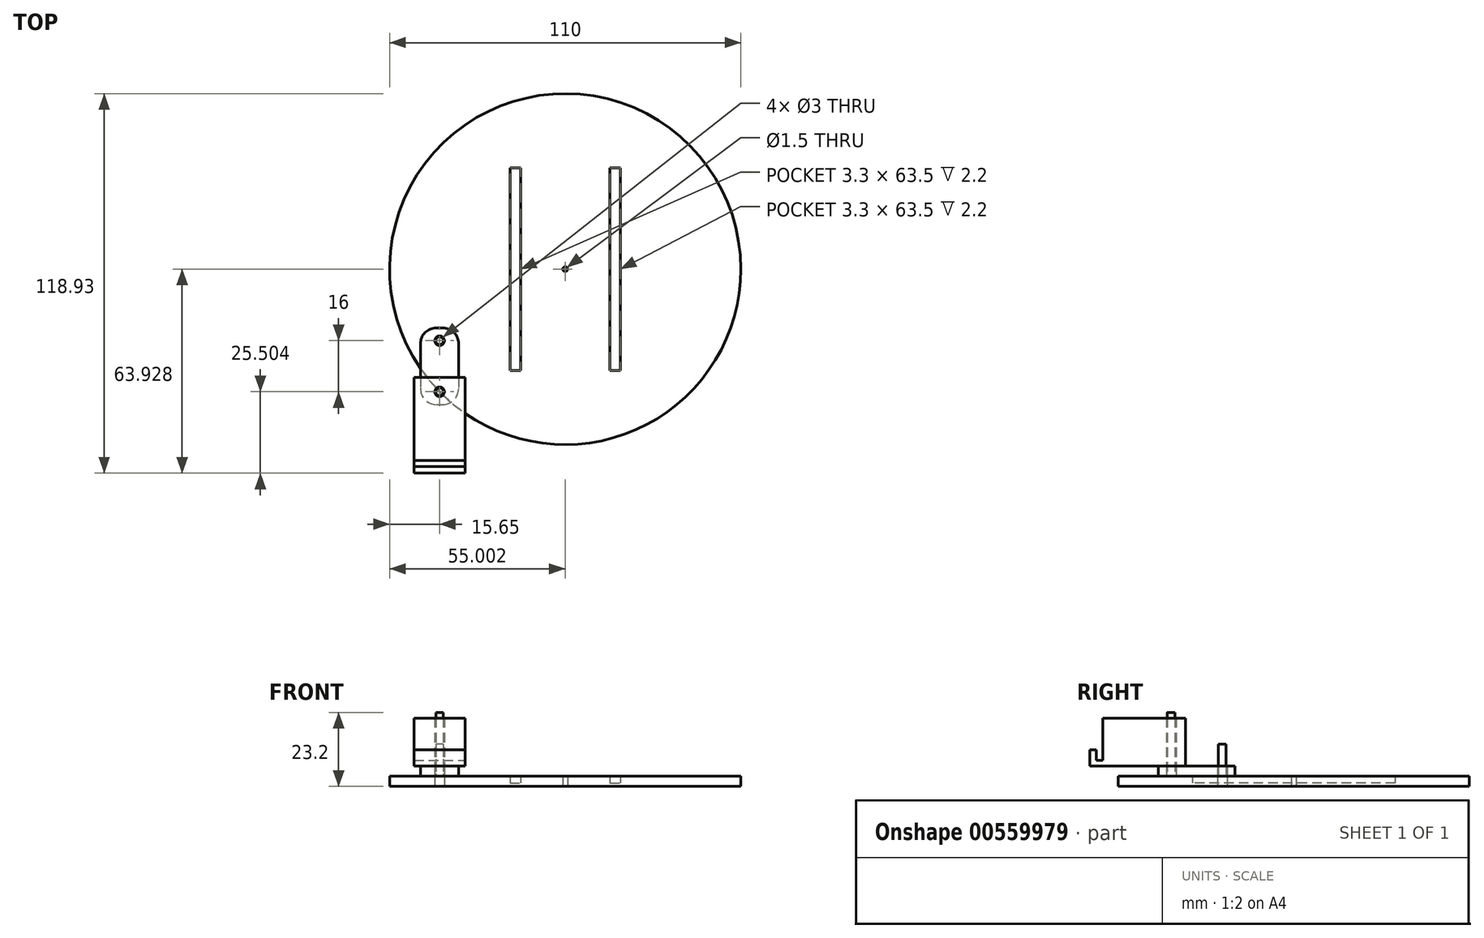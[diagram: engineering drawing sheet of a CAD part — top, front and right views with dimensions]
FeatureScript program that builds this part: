
annotation { "Feature Type Name" : "Feature", "Feature Type Description" : "" }
export const myFeature = defineFeature(function(context is Context, id is Id, definition is map)
    precondition{}
    {
        {
            var Q0;
            Q0=qCreatedBy(makeId("Top.planeOp"),FACE);
            var sketch = newSketch(context, id + "F0", { "sketchPlane" : qUnion([Q0])});
            skCircle(sketch, "E0", {"center": v(39.35, 117.44) * mm, "radius": 55 * mm});
            skCircle(sketch, "E1", {"center": v(0, 95.01) * mm, "radius": 1.5 * mm});
            skCircle(sketch, "E2", {"center": v(39.35, 117.44) * mm, "radius": 0.75 * mm});
            skLineSegment(sketch, "E3.bottom", {"start": v(22.05, 149.19) * mm, "end": v(25.35, 149.19) * mm});
            skLineSegment(sketch, "E3.top", {"start": v(22.05, 85.69) * mm, "end": v(25.35, 85.69) * mm});
            skLineSegment(sketch, "E3.left", {"start": v(22.05, 149.19) * mm, "end": v(22.05, 85.69) * mm});
            skLineSegment(sketch, "E3.right", {"start": v(25.35, 149.19) * mm, "end": v(25.35, 85.69) * mm});
            skLineSegment(sketch, "E4.bottom", {"start": v(53.35, 149.19) * mm, "end": v(56.65, 149.19) * mm});
            skLineSegment(sketch, "E4.top", {"start": v(53.35, 85.69) * mm, "end": v(56.65, 85.69) * mm});
            skLineSegment(sketch, "E4.left", {"start": v(53.35, 149.19) * mm, "end": v(53.35, 85.69) * mm});
            skLineSegment(sketch, "E4.right", {"start": v(56.65, 149.19) * mm, "end": v(56.65, 85.69) * mm});
            skSolve(sketch);
        }
        {
            var Q0;
            Q0=makeQuery(id+"F0.imprint","IMPRINT",FACE,{"disambiguationData":[TD([[makeQuery(id+"F0.imprint","IMPRINT",EDGE,{"derivedFrom":sQuery(id+"F0.wireOp",EDGE,"E0")}),1.0]])]});
            extrude(context, id + "F1", {"entities" : qUnion([Q0]), "depth" : 3.2 * mm});
        }
        {
            var Q0;
            Q0=makeQuery(id+"F0.imprint","IMPRINT",FACE,{"disambiguationData":[TD([[makeQuery(id+"F0.imprint","IMPRINT",EDGE,{"derivedFrom":sQuery(id+"F0.wireOp",EDGE,"E3.bottom")}),-1.0]])]});
            var Q1;
            Q1=makeQuery(id+"F0.imprint","IMPRINT",FACE,{"disambiguationData":[TD([[makeQuery(id+"F0.imprint","IMPRINT",EDGE,{"derivedFrom":sQuery(id+"F0.wireOp",EDGE,"E4.bottom")}),-1.0]])]});
            extrude(context, id + "F2", {"entities" : qUnion([Q0, Q1]), "operationType" : NewBodyOperationType.ADD, "depth" : 1 * mm});
        }
        {
            var Q0;
            Q0=makeQuery(id+"F1.opExtrude","CAP_FACE",FACE,{"disambiguationData":[OSD([sQuery(id+"F0.wireOp",EDGE,"E0"),sQuery(id+"F0.wireOp",EDGE,"E1"),sQuery(id+"F0.wireOp",EDGE,"E2"),sQuery(id+"F0.wireOp",EDGE,"E3.bottom"),sQuery(id+"F0.wireOp",EDGE,"E3.top"),sQuery(id+"F0.wireOp",EDGE,"E3.left"),sQuery(id+"F0.wireOp",EDGE,"E3.right"),sQuery(id+"F0.wireOp",EDGE,"E4.bottom"),sQuery(id+"F0.wireOp",EDGE,"E4.top"),sQuery(id+"F0.wireOp",EDGE,"E4.left"),sQuery(id+"F0.wireOp",EDGE,"E4.right")])],"isStart":false});
            var sketch = newSketch(context, id + "F3", { "sketchPlane" : qUnion([Q0])});
            skCircle(sketch, "E5", {"center": v(0, 95.01) * mm, "radius": 1.2 * mm});
            skSolve(sketch);
        }
        {
            var Q0;
            Q0=makeQuery(id+"F3.imprint","IMPRINT",FACE,{"disambiguationData":[TD([[makeQuery(id+"F3.imprint","IMPRINT",EDGE,{"derivedFrom":sQuery(id+"F3.wireOp",EDGE,"E5")}),1.0]])]});
            extrude(context, id + "F4", {"entities" : qUnion([Q0]), "depth" : 10 * mm, "offsetDistance" : 25 * mm});
        }
        {
            var Q0;
            Q0=makeQuery(id+"F1.opExtrude","CAP_FACE",FACE,{"disambiguationData":[OSD([sQuery(id+"F0.wireOp",EDGE,"E0"),sQuery(id+"F0.wireOp",EDGE,"E1"),sQuery(id+"F0.wireOp",EDGE,"E2"),sQuery(id+"F0.wireOp",EDGE,"E3.bottom"),sQuery(id+"F0.wireOp",EDGE,"E3.top"),sQuery(id+"F0.wireOp",EDGE,"E3.left"),sQuery(id+"F0.wireOp",EDGE,"E3.right"),sQuery(id+"F0.wireOp",EDGE,"E4.bottom"),sQuery(id+"F0.wireOp",EDGE,"E4.top"),sQuery(id+"F0.wireOp",EDGE,"E4.left"),sQuery(id+"F0.wireOp",EDGE,"E4.right")])],"isStart":false});
            var sketch = newSketch(context, id + "F5", { "sketchPlane" : qUnion([Q0])});
            skLineSegment(sketch, "E6.bottom", {"start": v(-6, 99.01) * mm, "end": v(6, 99.01) * mm});
            skLineSegment(sketch, "E6.top", {"start": v(-6, 75.01) * mm, "end": v(6, 75.01) * mm});
            skLineSegment(sketch, "E6.left", {"start": v(-6, 99.01) * mm, "end": v(-6, 75.01) * mm});
            skLineSegment(sketch, "E6.right", {"start": v(6, 99.01) * mm, "end": v(6, 75.01) * mm});
            skCircle(sketch, "E7", {"center": v(0, 95.01) * mm, "radius": 1.5 * mm});
            skCircle(sketch, "E8", {"center": v(0, 79.01) * mm, "radius": 1.5 * mm});
            skSolve(sketch);
        }
        {
            var Q0;
            {var subQ4=sQuery(id+"F5.wireOp",EDGE,"E6.top");var subQ6=sQuery(id+"F5.wireOp",EDGE,"E6.left");var subQ7=makeQuery(id+"F5.imprint","INTERSECT",VERTEX,{"derivedFrom":[subQ4,subQ6]});Q0=makeQuery(id+"F5.imprint","IMPRINT",FACE,{"disambiguationData":[TD([[makeQuery(id+"F5.imprint","IMPRINT",EDGE,{"disambiguationData":[TD([[subQ7,-1.0]])],"derivedFrom":subQ4}),1.0]])]});}
            var Q1;
            {var subQ1=sQuery(id+"F5.wireOp",EDGE,"E6.bottom");Q1=makeQuery(id+"F5.imprint","IMPRINT",FACE,{"disambiguationData":[TD([[makeQuery(id+"F5.imprint","IMPRINT",EDGE,{"derivedFrom":subQ1}),-1.0]])]});}
            extrude(context, id + "F6", {"entities" : qUnion([Q0, Q1]), "depth" : 3.2 * mm, "offsetDistance" : 25 * mm});
        }
        {
            var Q0;
            Q0=makeQuery(id+"F6.opExtrude","SWEPT_EDGE",EDGE,{"disambiguationData":[OSD([sQuery(id+"F5.wireOp",EDGE,"E6.bottom"),sQuery(id+"F5.wireOp",EDGE,"E6.left")])]});
            var Q1;
            Q1=makeQuery(id+"F6.opExtrude","SWEPT_EDGE",EDGE,{"disambiguationData":[OSD([sQuery(id+"F5.wireOp",EDGE,"E6.bottom"),sQuery(id+"F5.wireOp",EDGE,"E6.right")])]});
            var Q2;
            Q2=makeQuery(id+"F6.opExtrude","SWEPT_EDGE",EDGE,{"disambiguationData":[OSD([sQuery(id+"F5.wireOp",EDGE,"E6.top"),sQuery(id+"F5.wireOp",EDGE,"E6.right")])]});
            var Q3;
            Q3=makeQuery(id+"F6.opExtrude","SWEPT_EDGE",EDGE,{"disambiguationData":[OSD([sQuery(id+"F5.wireOp",EDGE,"E6.top"),sQuery(id+"F5.wireOp",EDGE,"E6.left")])]});
            fillet(context, id + "F7", {"entities" : qUnion([Q0, Q1, Q2, Q3]), "radius" : 5 * mm, "tangentPropagation" : true, "allowEdgeOverflow" : false});
        }
        {
            var Q0;
            Q0=makeQuery(id+"F1.opExtrude","CAP_FACE",FACE,{"disambiguationData":[OSD([sQuery(id+"F0.wireOp",EDGE,"E0"),sQuery(id+"F0.wireOp",EDGE,"E1"),sQuery(id+"F0.wireOp",EDGE,"E2"),sQuery(id+"F0.wireOp",EDGE,"E3.bottom"),sQuery(id+"F0.wireOp",EDGE,"E3.top"),sQuery(id+"F0.wireOp",EDGE,"E3.left"),sQuery(id+"F0.wireOp",EDGE,"E3.right"),sQuery(id+"F0.wireOp",EDGE,"E4.bottom"),sQuery(id+"F0.wireOp",EDGE,"E4.top"),sQuery(id+"F0.wireOp",EDGE,"E4.left"),sQuery(id+"F0.wireOp",EDGE,"E4.right")])],"isStart":false});
            var sketch = newSketch(context, id + "F8", { "sketchPlane" : qUnion([Q0])});
            skCircle(sketch, "E9", {"center": v(0, 79.01) * mm, "radius": 1.2 * mm});
            skSolve(sketch);
        }
        {
            var Q0;
            {var subQ0=sQuery(id+"F8.wireOp",EDGE,"E9");var subQ1=makeQuery(id+"F1.opExtrude","CAP_EDGE",EDGE,{"disambiguationData":[OSD([sQuery(id+"F0.wireOp",EDGE,"E0")])],"isStart":false});var subQ2=makeQuery(id+"F8.imprint","INTERSECT",VERTEX,{"disambiguationData":[OD(0.0)],"derivedFrom":[subQ1,subQ0]});Q0=makeQuery(id+"F8.imprint","IMPRINT",FACE,{"disambiguationData":[TD([[makeQuery(id+"F8.imprint","IMPRINT",EDGE,{"disambiguationData":[TD([[subQ2,-1.0]])],"derivedFrom":subQ0}),1.0]])]});}
            var Q1;
            {var subQ0=sQuery(id+"F8.wireOp",EDGE,"E9");var subQ1=makeQuery(id+"F1.opExtrude","CAP_EDGE",EDGE,{"disambiguationData":[OSD([sQuery(id+"F0.wireOp",EDGE,"E0")])],"isStart":false});var subQ2=makeQuery(id+"F8.imprint","INTERSECT",VERTEX,{"disambiguationData":[OD(0.0)],"derivedFrom":[subQ1,subQ0]});Q1=makeQuery(id+"F8.imprint","IMPRINT",FACE,{"disambiguationData":[TD([[makeQuery(id+"F8.imprint","IMPRINT",EDGE,{"disambiguationData":[TD([[subQ2,1.0]])],"derivedFrom":subQ0}),1.0]])]});}
            extrude(context, id + "F9", {"entities" : qUnion([Q0, Q1]), "depth" : 20 * mm, "offsetDistance" : 25 * mm});
        }
        {
            var Q0;
            Q0=makeQuery(id+"F6.opExtrude","CAP_FACE",FACE,{"disambiguationData":[OSD([sQuery(id+"F5.wireOp",EDGE,"E6.bottom"),sQuery(id+"F5.wireOp",EDGE,"E6.top"),sQuery(id+"F5.wireOp",EDGE,"E6.left"),sQuery(id+"F5.wireOp",EDGE,"E6.right"),sQuery(id+"F5.wireOp",EDGE,"E7"),sQuery(id+"F5.wireOp",EDGE,"E8")])],"isStart":false});
            var sketch = newSketch(context, id + "F10", { "sketchPlane" : qUnion([Q0])});
            skLineSegment(sketch, "E10.bottom", {"start": v(-8, 83.51) * mm, "end": v(8, 83.51) * mm});
            skLineSegment(sketch, "E10.top", {"start": v(-8, 53.51) * mm, "end": v(8, 53.51) * mm});
            skLineSegment(sketch, "E10.left", {"start": v(-8, 83.51) * mm, "end": v(-8, 53.51) * mm});
            skLineSegment(sketch, "E10.right", {"start": v(8, 83.51) * mm, "end": v(8, 53.51) * mm});
            skCircle(sketch, "E11", {"center": v(0, 79.01) * mm, "radius": 1.5 * mm});
            skSolve(sketch);
        }
        {
            var Q0;
            Q0=makeQuery(id+"F10.imprint","IMPRINT",FACE,{"disambiguationData":[TD([[makeQuery(id+"F10.imprint","IMPRINT",EDGE,{"derivedFrom":sQuery(id+"F10.wireOp",EDGE,"E10.top")}),1.0]])]});
            var Q1;
            Q1=makeQuery(id+"F10.imprint","IMPRINT",FACE,{"disambiguationData":[TD([[makeQuery(id+"F10.imprint","IMPRINT",EDGE,{"derivedFrom":sQuery(id+"F10.wireOp",EDGE,"E11")}),-1.0]])]});
            extrude(context, id + "F11", {"entities" : qUnion([Q0, Q1]), "depth" : 15 * mm, "offsetDistance" : 25 * mm});
        }
        {
            var Q0;
            Q0=makeQuery(id+"F11.opExtrude","SWEPT_FACE",FACE,{"disambiguationData":[OSD([sQuery(id+"F10.wireOp",EDGE,"E10.right")])]});
            var sketch = newSketch(context, id + "F12", { "sketchPlane" : qUnion([Q0])});
            skLineSegment(sketch, "E12.bottom", {"start": v(53.51, 21.4) * mm, "end": v(57.51, 21.4) * mm});
            skLineSegment(sketch, "E12.right", {"start": v(57.51, 21.4) * mm, "end": v(57.51, 8.2) * mm});
            skLineSegment(sketch, "E13.top", {"start": v(53.51, 11.48) * mm, "end": v(55.51, 11.48) * mm});
            skLineSegment(sketch, "E13.right", {"start": v(55.51, 8.2) * mm, "end": v(55.51, 11.48) * mm});
            skLineSegment(sketch, "E14", {"start": v(55.51, 8.2) * mm, "end": v(57.51, 8.2) * mm});
            skLineSegment(sketch, "E15", {"start": v(53.51, 21.4) * mm, "end": v(53.51, 11.48) * mm});
            skSolve(sketch);
        }
        {
            var Q0;
            Q0=makeQuery(id+"F12.imprint","IMPRINT",FACE,{"disambiguationData":[TD([[makeQuery(id+"F12.imprint","IMPRINT",EDGE,{"derivedFrom":sQuery(id+"F12.wireOp",EDGE,"E12.bottom")}),1.0]])]});
            extrude(context, id + "F13", {"entities" : qUnion([Q0]), "operationType" : NewBodyOperationType.REMOVE, "oppositeDirection" : true, "depth" : 25 * mm, "offsetDistance" : 25 * mm});
        }
    });
